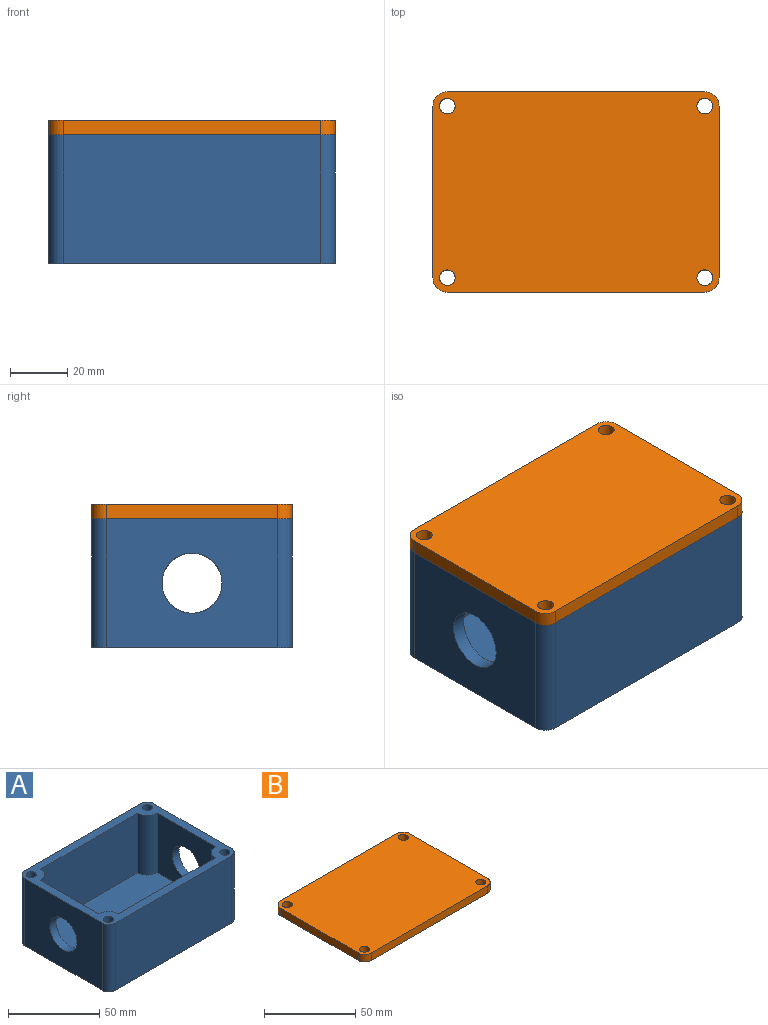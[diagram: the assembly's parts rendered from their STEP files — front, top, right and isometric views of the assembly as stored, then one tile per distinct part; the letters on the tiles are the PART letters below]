
ASSEMBLY  parts=2 mates=1
PART A: 25 faces, bbox 100x70x45 mm
  f0: plane 45x40mm, normal (1,0,0), area 1453.6mm2, adj f1,f9,f13,f14,f20
  f1: plane 90x60mm, normal (0,0,1), area 5223.3mm2, adj f0,f2,f3,f4,f11,f12,f13,f14
  f2: plane 75x40mm, normal (0,1,0), area 3000mm2, adj f1,f9,f12,f14
  f3: plane 45x40mm, normal (-1,0,0), area 1453.6mm2, adj f1,f9,f11,f12,f19
  f4: plane 75x40mm, normal (0,-1,0), area 3000mm2, adj f1,f9,f11,f13
  f5: plane 60x45mm, normal (-1,0,0), area 2353.6mm2, adj f9,f10,f20,f21,f24
  f6: plane 90x45mm, normal (0,-1,0), area 4050mm2, adj f9,f10,f21,f22
  f7: plane 60x45mm, normal (1,0,0), area 2353.6mm2, adj f9,f10,f19,f22,f23
  f8: plane 90x45mm, normal (0,1,0), area 4050mm2, adj f9,f10,f23,f24
  f9: plane 100x70mm, normal (0,0,1), area 1660.2mm2, adj f0,f2,f3,f4,f5,f6,f7,f8
  f10: plane 100x70mm, normal (0,0,-1), area 6883.5mm2, adj f5,f6,f7,f8,f15,f16,f17,f18
  f11: cylinder r=7.5mm len=40mm, axis (0,0,-1), area 471.2mm2, adj f1,f3,f4,f9
  f12: cylinder r=7.5mm len=40mm, axis (0,0,-1), area 471.2mm2, adj f1,f2,f3,f9
  f13: cylinder r=7.5mm len=40mm, axis (0,0,-1), area 471.2mm2, adj f0,f1,f4,f9
  f14: cylinder r=7.5mm len=40mm, axis (0,0,-1), area 471.2mm2, adj f0,f1,f2,f9
  f15: cylinder r=2.75mm len=45mm, axis (0,0,1), area 777.5mm2, adj f9,f10
  f16: cylinder r=2.75mm len=45mm, axis (0,0,1), area 777.5mm2, adj f9,f10
  f17: cylinder r=2.75mm len=45mm, axis (0,0,1), area 777.5mm2, adj f9,f10
  f18: cylinder r=2.75mm len=45mm, axis (0,0,1), area 777.5mm2, adj f9,f10
  f19: cylinder r=10.5mm len=21mm, axis (-1,0,0), area 329.9mm2, adj f3,f7
  f20: cylinder r=10.5mm len=21mm, axis (-1,0,0), area 329.9mm2, adj f0,f5
  f21: cylinder r=5mm len=45mm, axis (0,0,-1), area 353.4mm2, adj f5,f6,f9,f10
  f22: cylinder r=5mm len=45mm, axis (0,0,1), area 353.4mm2, adj f6,f7,f9,f10
  f23: cylinder r=5mm len=45mm, axis (0,0,-1), area 353.4mm2, adj f7,f8,f9,f10
  f24: cylinder r=5mm len=45mm, axis (0,0,1), area 353.4mm2, adj f5,f8,f9,f10
PART B: 14 faces, bbox 100x70x5 mm
  f0: plane 90x5mm, normal (0,-1,0), area 450mm2, adj f4,f5,f6,f9
  f1: plane 60x5mm, normal (1,0,0), area 300mm2, adj f4,f5,f6,f7
  f2: plane 90x5mm, normal (0,1,0), area 450mm2, adj f4,f5,f7,f8
  f3: plane 60x5mm, normal (-1,0,0), area 300mm2, adj f4,f5,f8,f9
  f4: plane 100x70mm, normal (0,0,-1), area 6883.5mm2, adj f0,f1,f2,f3,f6,f7,f8,f9
  f5: plane 100x70mm, normal (0,0,1), area 6883.5mm2, adj f0,f1,f2,f3,f6,f7,f8,f9
  f6: cylinder r=5mm len=5mm, axis (0,0,1), area 39.3mm2, adj f0,f1,f4,f5
  f7: cylinder r=5mm len=5mm, axis (0,0,1), area 39.3mm2, adj f1,f2,f4,f5
  f8: cylinder r=5mm len=5mm, axis (0,0,1), area 39.3mm2, adj f2,f3,f4,f5
  f9: cylinder r=5mm len=5mm, axis (0,0,1), area 39.3mm2, adj f0,f3,f4,f5
  f10: cylinder r=2.75mm len=5.5mm, axis (0,0,1), area 86.4mm2, adj f4,f5
  f11: cylinder r=2.75mm len=5.5mm, axis (0,0,1), area 86.4mm2, adj f4,f5
  f12: cylinder r=2.75mm len=5.5mm, axis (0,0,1), area 86.4mm2, adj f4,f5
  f13: cylinder r=2.75mm len=5.5mm, axis (0,0,1), area 86.4mm2, adj f4,f5
PLACE A t=(-0.42,-2.54,-2.86)mm
PLACE B t=(-0.86,-3.03,47.14)mm
MATE fastened B.f4 <-> A.f9  axis (0,0,-1) through (-0.86,-3.03,42.14)mm
